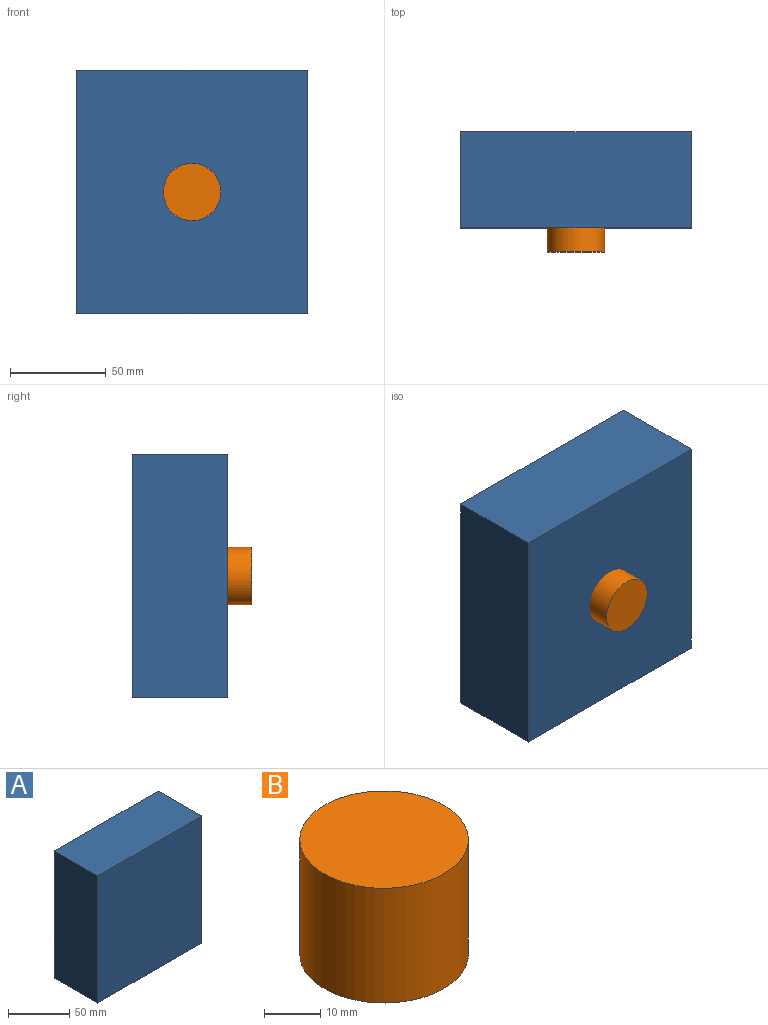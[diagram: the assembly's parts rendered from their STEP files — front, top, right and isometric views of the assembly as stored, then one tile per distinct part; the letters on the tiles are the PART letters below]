
ASSEMBLY  parts=2 mates=1
PART A: 6 faces, bbox 120x50x127 mm
  f0: plane 127x120mm, normal (0,1,0), area 15240mm2, adj f1,f3,f4,f5
  f1: plane 127x50mm, normal (-1,0,0), area 6350mm2, adj f0,f2,f4,f5
  f2: plane 127x120mm, normal (0,-1,0), area 15240mm2, adj f1,f3,f4,f5
  f3: plane 127x50mm, normal (1,0,0), area 6350mm2, adj f0,f2,f4,f5
  f4: plane 120x50mm, normal (0,0,1), area 6000mm2, adj f0,f1,f2,f3
  f5: plane 120x50mm, normal (0,0,-1), area 6000mm2, adj f0,f1,f2,f3
PART B: 3 faces, bbox 30x30x25 mm
  f0: cylinder r=15mm len=30mm, axis (0,0,-1), area 2356.2mm2, adj f1,f2
  f1: plane 30x30mm, normal (0,0,1), area 706.9mm2, adj f0
  f2: plane 30x30mm, normal (0,0,-1), area 706.9mm2, adj f0
PLACE A t=(-76.35,0.5,-23.72)mm fixed
PLACE B rot(axis=(-1,0,0),90deg) t=(-33.59,-51.81,129.87)mm
MATE cylindrical A.f2 <-> B.f0  axis (0,-1,0) through (-73.53,-39.31,39.78)mm
